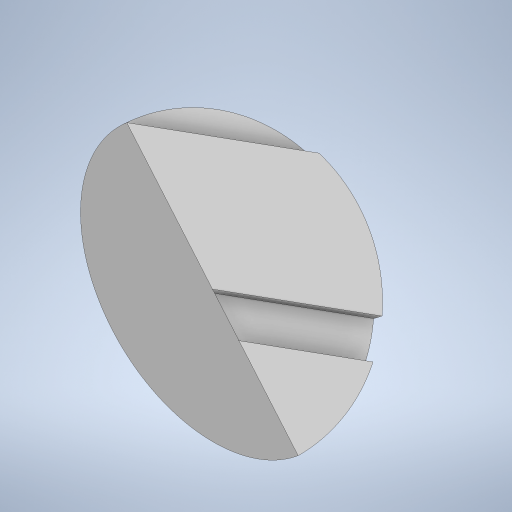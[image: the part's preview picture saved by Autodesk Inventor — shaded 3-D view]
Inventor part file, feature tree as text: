
AUTODESK INVENTOR PART (.ipt)
format: ipt  version: 2024 (Build 280153000, 153)  size: 241,152 bytes
history: native  units: mm
features: sketch x2, revolve x1, emboss x1
ambient origin geometry x8: Origin, YZ Plane, XZ Plane, XY Plane, X Axis, Y Axis, Z Axis, Center Point
bodies: Solid1 (feature_tree)
feature tree (4):
  sketch  "Sketch1"  dims[d1=17.453293mm d2=1.0mm d3=0.0mm]
  revolve  "Revolution1"  [1 undecoded]
  emboss  "Emboss1"
  sketch  "Sketch2"
note: 1 required parameter value undecoded (feature->parameter linkage not recoverable at this tier; creation-order binding heuristic only, values carry confidence <= 0.55)
